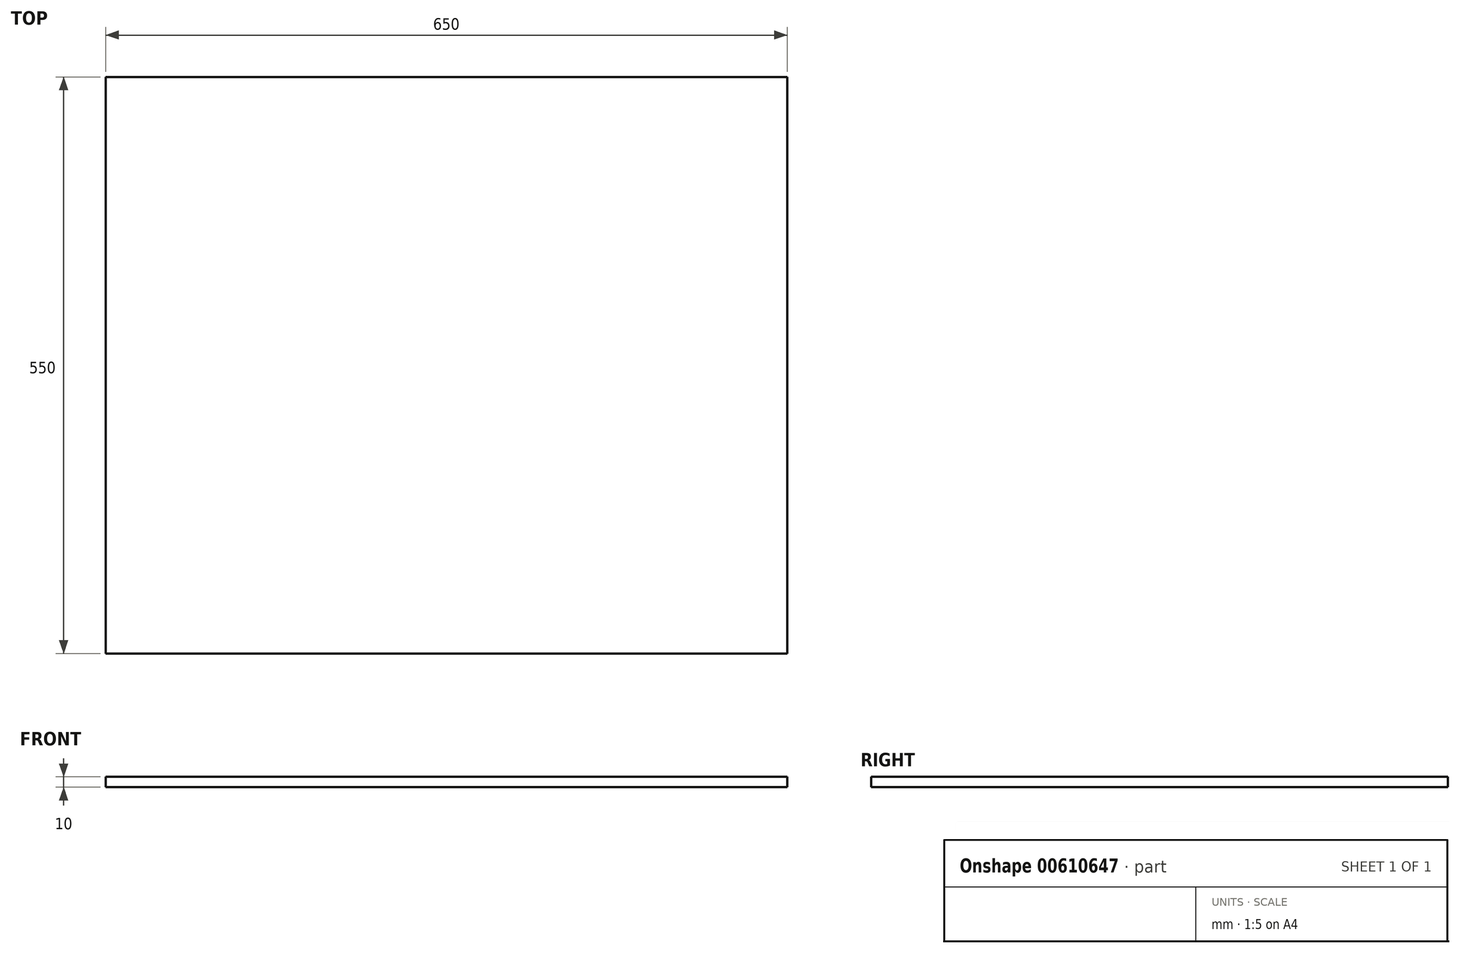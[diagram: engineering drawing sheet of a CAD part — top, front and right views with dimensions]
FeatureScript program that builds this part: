
annotation { "Feature Type Name" : "Feature", "Feature Type Description" : "" }
export const myFeature = defineFeature(function(context is Context, id is Id, definition is map)
    precondition{}
    {
        {
            var Q0;
            Q0=qCreatedBy(makeId("Top.planeOp"),FACE);
            var sketch = newSketch(context, id + "F0", { "sketchPlane" : qUnion([Q0])});
            skLineSegment(sketch, "E0.bottom", {"start": v(-336.36, 226.6) * mm, "end": v(313.64, 226.6) * mm});
            skLineSegment(sketch, "E0.top", {"start": v(-336.36, -323.4) * mm, "end": v(313.64, -323.4) * mm});
            skLineSegment(sketch, "E0.left", {"start": v(-336.36, 226.6) * mm, "end": v(-336.36, -323.4) * mm});
            skLineSegment(sketch, "E0.right", {"start": v(313.64, 226.6) * mm, "end": v(313.64, -323.4) * mm});
            skSolve(sketch);
        }
        {
            var Q0;
            Q0=makeQuery(id+"F0.imprint","IMPRINT",FACE,{"disambiguationData":[TD([[makeQuery(id+"F0.imprint","IMPRINT",EDGE,{"derivedFrom":sQuery(id+"F0.wireOp",EDGE,"E0.bottom")}),-1.0]])]});
            extrude(context, id + "F1", {"entities" : qUnion([Q0]), "depth" : 10 * mm, "offsetDistance" : 25 * mm});
        }
    });
